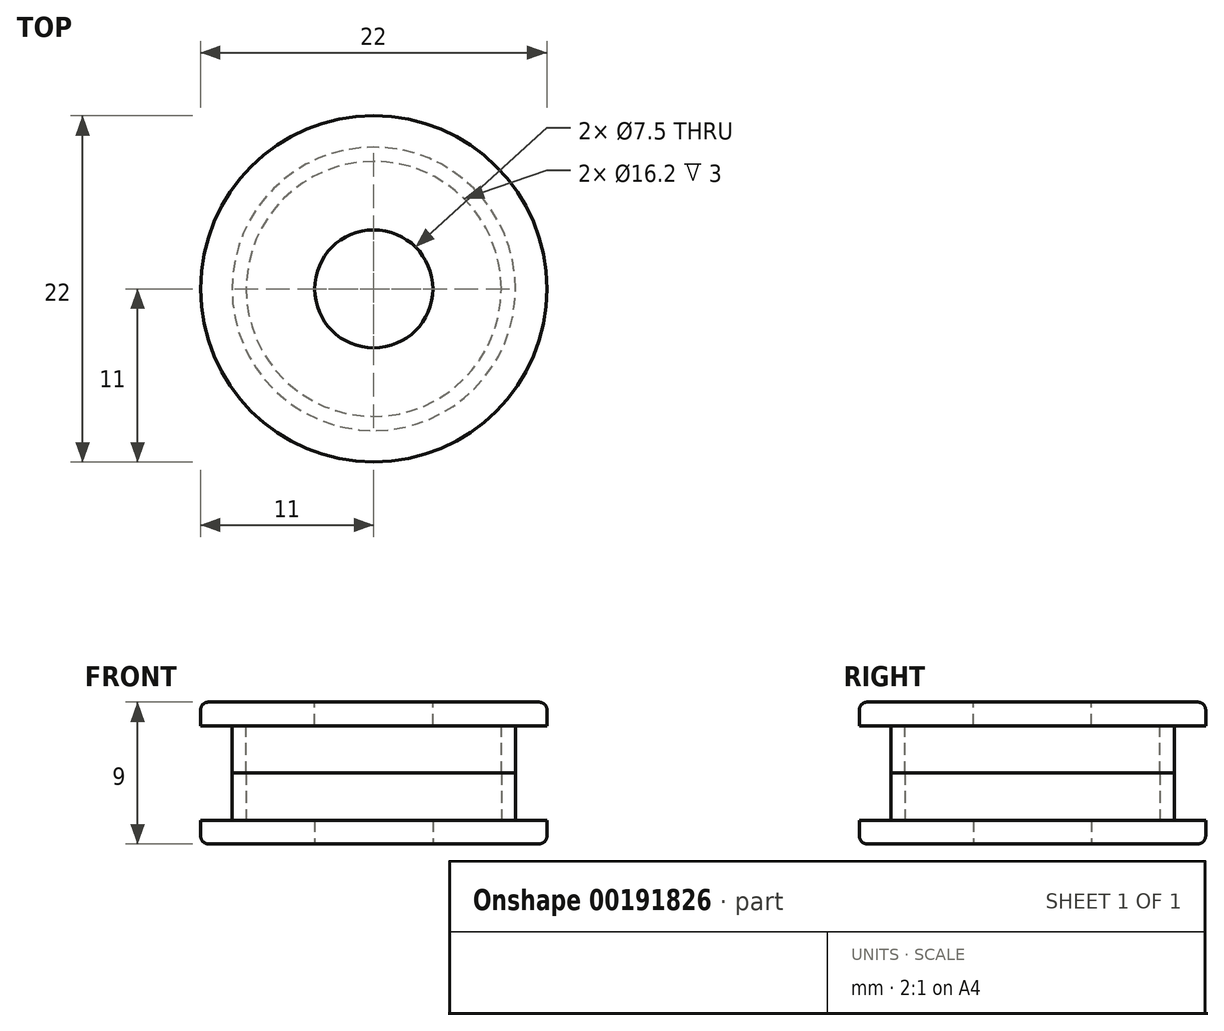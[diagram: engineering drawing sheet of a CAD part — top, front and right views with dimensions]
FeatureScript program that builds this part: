
annotation { "Feature Type Name" : "Feature", "Feature Type Description" : "" }
export const myFeature = defineFeature(function(context is Context, id is Id, definition is map)
    precondition{}
    {
        {
            var Q0;
            Q0=qCreatedBy(makeId("Top.planeOp"),FACE);
            var sketch = newSketch(context, id + "F0", { "sketchPlane" : qUnion([Q0])});
            skCircle(sketch, "E0", {"center": v(0, 0) * mm, "radius": 11 * mm});
            skCircle(sketch, "E1", {"center": v(0, 0) * mm, "radius": 3.75 * mm});
            skSolve(sketch);
        }
        {
            var Q0;
            Q0=makeQuery(id+"F0.imprint","IMPRINT",FACE,{"disambiguationData":[TD([[makeQuery(id+"F0.imprint","IMPRINT",EDGE,{"derivedFrom":sQuery(id+"F0.wireOp",EDGE,"E0")}),1.0]])]});
            extrude(context, id + "F1", {"entities" : qUnion([Q0]), "depth" : 1.5 * mm});
        }
        {
            var Q0;
            Q0=makeQuery(id+"F1.opExtrude","CAP_FACE",FACE,{"disambiguationData":[OSD([sQuery(id+"F0.wireOp",EDGE,"E0"),sQuery(id+"F0.wireOp",EDGE,"E1")])],"isStart":false});
            var sketch = newSketch(context, id + "F2", { "sketchPlane" : qUnion([Q0])});
            skCircle(sketch, "E2", {"center": v(0, 0) * mm, "radius": 8.1 * mm});
            skCircle(sketch, "E3", {"center": v(0, 0) * mm, "radius": 9 * mm});
            skSolve(sketch);
        }
        {
            var Q0;
            Q0=makeQuery(id+"F2.imprint","IMPRINT",FACE,{"disambiguationData":[TD([[makeQuery(id+"F2.imprint","IMPRINT",EDGE,{"derivedFrom":sQuery(id+"F2.wireOp",EDGE,"E2")}),-1.0]])]});
            extrude(context, id + "F3", {"entities" : qUnion([Q0]), "operationType" : NewBodyOperationType.ADD, "depth" : 3 * mm});
        }
        {
            var Q0;
            Q0=makeQuery(id+"F1.opExtrude","SWEPT_BODY",BODY,{"disambiguationData":[OSD([sQuery(id+"F0.wireOp",EDGE,"E0"),sQuery(id+"F0.wireOp",EDGE,"E1")])]});
            var Q1;
            Q1=makeQuery(id+"F3.opExtrude","CAP_FACE",FACE,{"disambiguationData":[OSD([sQuery(id+"F2.wireOp",EDGE,"E2"),sQuery(id+"F2.wireOp",EDGE,"E3")])],"isStart":false});
            mirror(context, id + "F4", {"entities" : qUnion([Q0]), "mirrorPlane" : qUnion([Q1])});
        }
        {
            var Q0;
            Q0=makeQuery(id+"F4.opPattern","COPY",EDGE,{"derivedFrom":makeQuery(id+"F1.opExtrude","CAP_EDGE",EDGE,{"disambiguationData":[OSD([sQuery(id+"F0.wireOp",EDGE,"E0")])],"isStart":true}),"instanceName":"1"});
            var Q1;
            Q1=makeQuery(id+"F1.opExtrude","CAP_EDGE",EDGE,{"disambiguationData":[OSD([sQuery(id+"F0.wireOp",EDGE,"E0")])],"isStart":true});
            fillet(context, id + "F5", {"entities" : qUnion([Q0, Q1]), "radius" : 0.5 * mm, "tangentPropagation" : true, "allowEdgeOverflow" : false});
        }
    });
